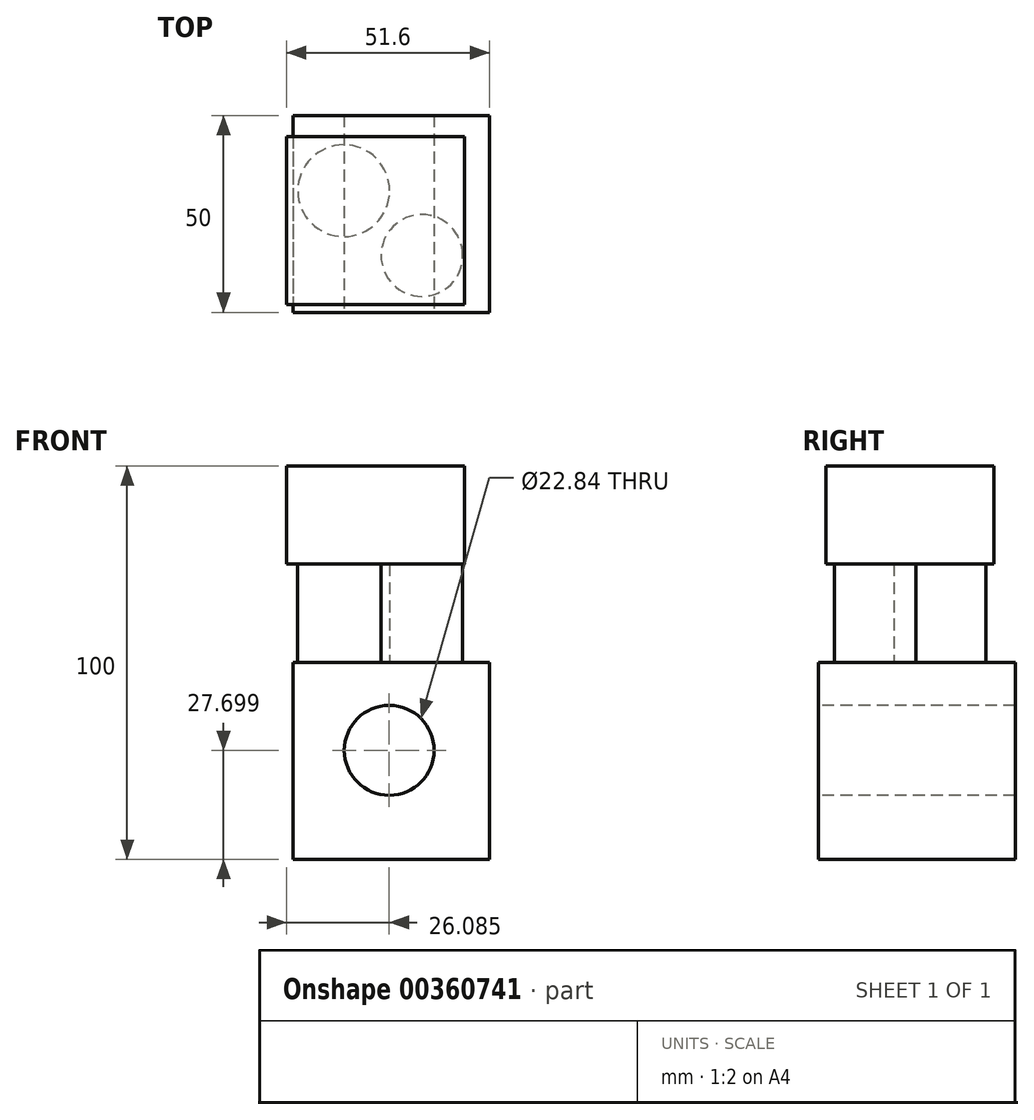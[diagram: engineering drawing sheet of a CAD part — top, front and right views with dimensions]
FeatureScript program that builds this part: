
annotation { "Feature Type Name" : "Feature", "Feature Type Description" : "" }
export const myFeature = defineFeature(function(context is Context, id is Id, definition is map)
    precondition{}
    {
        {
            var Q0;
            Q0=qCreatedBy(makeId("Top.planeOp"),FACE);
            var sketch = newSketch(context, id + "F0", { "sketchPlane" : qUnion([Q0])});
            skLineSegment(sketch, "E0.bottom", {"start": v(0, 50) * mm, "end": v(50, 50) * mm});
            skLineSegment(sketch, "E0.top", {"start": v(0, 0) * mm, "end": v(50, 0) * mm});
            skLineSegment(sketch, "E0.left", {"start": v(0, 50) * mm, "end": v(0, 0) * mm});
            skLineSegment(sketch, "E0.right", {"start": v(50, 50) * mm, "end": v(50, 0) * mm});
            skSolve(sketch);
        }
        {
            var Q0;
            Q0 = qSketchRegion(id + "F0", true);
            extrude(context, id + "F1", {"entities" : qUnion([Q0]), "depth" : 50 * mm});
        }
        {
            var Q0;
            Q0=makeQuery(id+"F1.opExtrude","CAP_FACE",FACE,{"disambiguationData":[OSD([sQuery(id+"F0.wireOp",EDGE,"E0.bottom"),sQuery(id+"F0.wireOp",EDGE,"E0.top"),sQuery(id+"F0.wireOp",EDGE,"E0.left"),sQuery(id+"F0.wireOp",EDGE,"E0.right")])],"isStart":false});
            var sketch = newSketch(context, id + "F2", { "sketchPlane" : qUnion([Q0])});
            skCircle(sketch, "E1", {"center": v(12.92, 30.9) * mm, "radius": 11.66 * mm});
            skSolve(sketch);
        }
        {
            var Q0;
            Q0 = qSketchRegion(id + "F2", true);
            extrude(context, id + "F3", {"entities" : qUnion([Q0]), "operationType" : NewBodyOperationType.ADD, "depth" : 25 * mm});
        }
        {
            var Q0;
            Q0=makeQuery(id+"F1.opExtrude","CAP_FACE",FACE,{"disambiguationData":[OSD([sQuery(id+"F0.wireOp",EDGE,"E0.bottom"),sQuery(id+"F0.wireOp",EDGE,"E0.top"),sQuery(id+"F0.wireOp",EDGE,"E0.left"),sQuery(id+"F0.wireOp",EDGE,"E0.right")])],"isStart":false});
            var sketch = newSketch(context, id + "F4", { "sketchPlane" : qUnion([Q0])});
            skCircle(sketch, "E2", {"center": v(32.78, 14.44) * mm, "radius": 10.38 * mm});
            skSolve(sketch);
        }
        {
            var Q0;
            Q0 = qSketchRegion(id + "F4", true);
            extrude(context, id + "F5", {"entities" : qUnion([Q0]), "operationType" : NewBodyOperationType.ADD, "depth" : 25 * mm});
        }
        {
            var Q0;
            Q0=makeQuery(id+"F5.opExtrude","CAP_FACE",FACE,{"disambiguationData":[OSD([sQuery(id+"F4.wireOp",EDGE,"E2")])],"isStart":false});
            var sketch = newSketch(context, id + "F6", { "sketchPlane" : qUnion([Q0])});
            skLineSegment(sketch, "E3.bottom", {"start": v(43.55, 44.6) * mm, "end": v(-1.6, 44.6) * mm});
            skLineSegment(sketch, "E3.top", {"start": v(43.55, 1.97) * mm, "end": v(-1.6, 1.97) * mm});
            skLineSegment(sketch, "E3.left", {"start": v(43.55, 44.6) * mm, "end": v(43.55, 1.97) * mm});
            skLineSegment(sketch, "E3.right", {"start": v(-1.6, 44.6) * mm, "end": v(-1.6, 1.97) * mm});
            skSolve(sketch);
        }
        {
            var Q0;
            Q0=makeQuery(id+"F6.imprint","IMPRINT",FACE,{"disambiguationData":[TD([[makeQuery(id+"F6.imprint","IMPRINT",EDGE,{"derivedFrom":makeQuery(id+"F5.opExtrude","CAP_EDGE",EDGE,{"disambiguationData":[OSD([sQuery(id+"F4.wireOp",EDGE,"E2")])],"isStart":false})}),1.0]])]});
            var Q1;
            Q1=makeQuery(id+"F6.imprint","IMPRINT",FACE,{"disambiguationData":[TD([[makeQuery(id+"F6.imprint","IMPRINT",EDGE,{"derivedFrom":sQuery(id+"F6.wireOp",EDGE,"E3.bottom")}),1.0]])]});
            extrude(context, id + "F7", {"entities" : qUnion([Q0, Q1]), "operationType" : NewBodyOperationType.ADD, "depth" : 25 * mm});
        }
        {
            var Q0;
            Q0=makeQuery(id+"F1.opExtrude","SWEPT_FACE",FACE,{"disambiguationData":[OSD([sQuery(id+"F0.wireOp",EDGE,"E0.top")])]});
            var sketch = newSketch(context, id + "F8", { "sketchPlane" : qUnion([Q0])});
            skCircle(sketch, "E4", {"center": v(24.49, 27.7) * mm, "radius": 11.42 * mm});
            skSolve(sketch);
        }
        {
            var Q0;
            Q0 = qSketchRegion(id + "F8", true);
            extrude(context, id + "F9", {"entities" : qUnion([Q0]), "operationType" : NewBodyOperationType.REMOVE, "oppositeDirection" : true, "depth" : 162 * mm});
        }
    });
